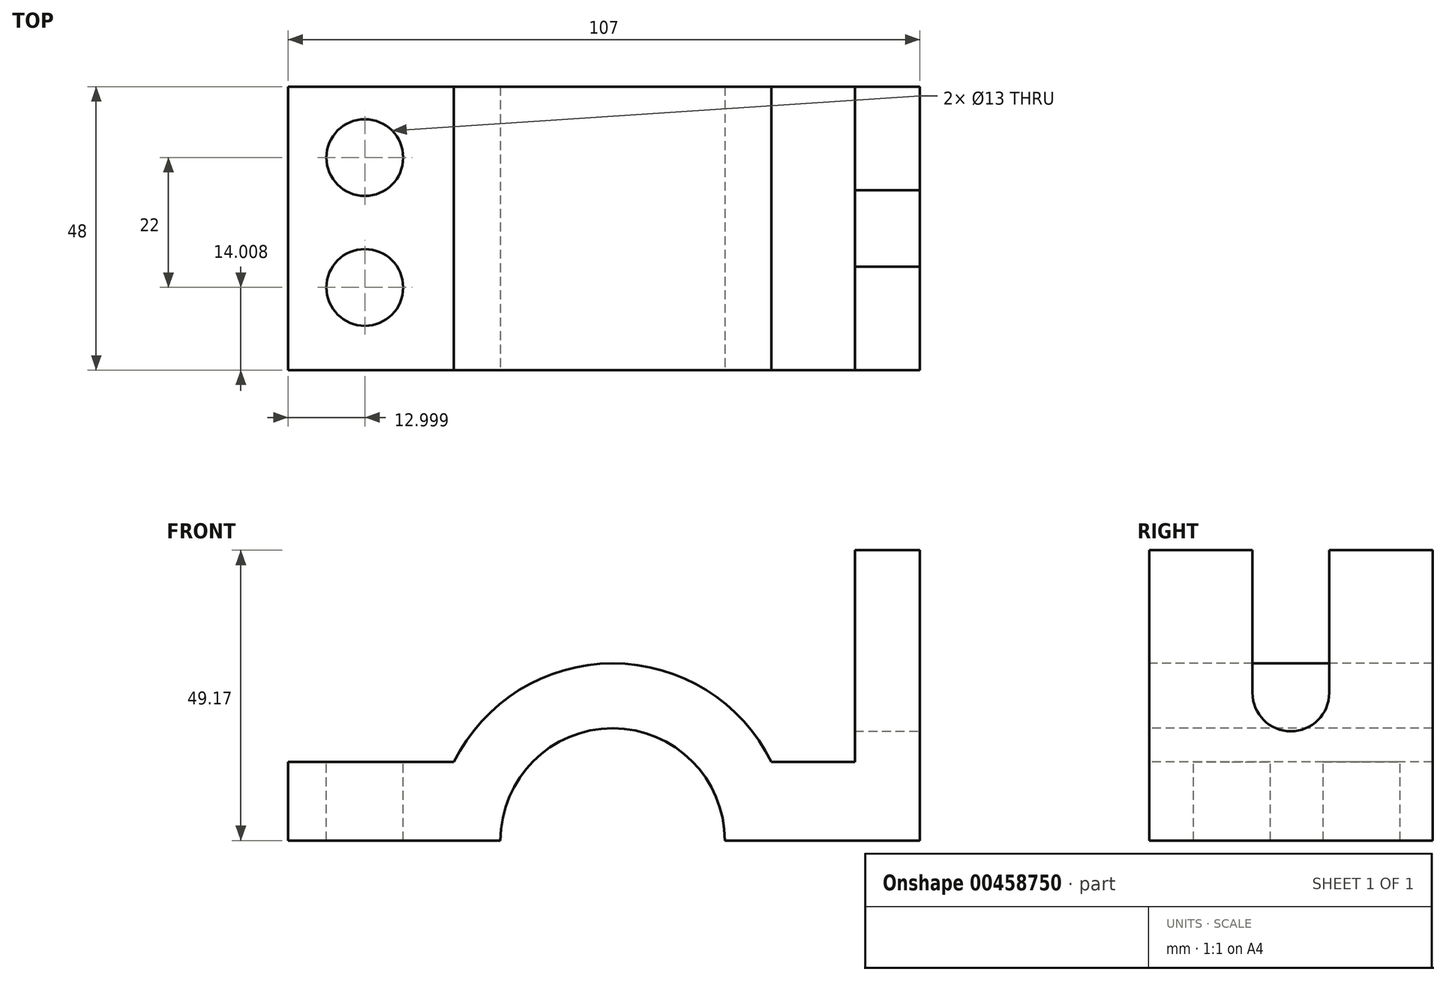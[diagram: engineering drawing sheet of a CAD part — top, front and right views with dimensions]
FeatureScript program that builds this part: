
annotation { "Feature Type Name" : "Feature", "Feature Type Description" : "" }
export const myFeature = defineFeature(function(context is Context, id is Id, definition is map)
    precondition{}
    {
        {
            var Q0;
            Q0=qCreatedBy(makeId("Front.planeOp"),FACE);
            var sketch = newSketch(context, id + "F0", { "sketchPlane" : qUnion([Q0])});
            skLineSegment(sketch, "E0", {"start": v(-19, 0) * mm, "end": v(-54.98, 0) * mm});
            skLineSegment(sketch, "E1", {"start": v(-54.98, 0) * mm, "end": v(-54.98, 13.3) * mm});
            skLineSegment(sketch, "E2", {"start": v(-54.98, 13.3) * mm, "end": v(-26.9, 13.3) * mm});
            skLineSegment(sketch, "E3", {"start": v(19, 0) * mm, "end": v(52.02, 0) * mm});
            skLineSegment(sketch, "E4", {"start": v(52.02, 0) * mm, "end": v(52.02, 49.17) * mm});
            skLineSegment(sketch, "E5", {"start": v(52.02, 49.17) * mm, "end": v(41.02, 49.17) * mm});
            skLineSegment(sketch, "E6", {"start": v(41.02, 49.17) * mm, "end": v(41.02, 13.3) * mm});
            skLineSegment(sketch, "E7", {"start": v(41.02, 13.3) * mm, "end": v(26.9, 13.3) * mm});
            skArc(sketch, "E8", {"start": v(19, 0) * mm, "mid": v(0, 19) * mm, "end": v(-19, 0) * mm});
            skArc(sketch, "E9", {"start": v(26.9, 13.3) * mm, "mid": v(0, 30) * mm, "end": v(-26.9, 13.3) * mm});
            skSolve(sketch);
        }
        {
            var Q0;
            Q0 = qSketchRegion(id + "F0", true);
            extrude(context, id + "F1", {"entities" : qUnion([Q0]), "oppositeDirection" : true, "depth" : 48 * mm});
        }
        {
            var Q0;
            Q0=makeQuery(id+"F1.opExtrude","SWEPT_FACE",FACE,{"disambiguationData":[OSD([sQuery(id+"F0.wireOp",EDGE,"E4")])]});
            var sketch = newSketch(context, id + "F2", { "sketchPlane" : qUnion([Q0])});
            skLineSegment(sketch, "E10", {"start": v(17.5, 49.17) * mm, "end": v(17.5, 25) * mm});
            skLineSegment(sketch, "E11", {"start": v(30.5, 49.17) * mm, "end": v(30.5, 25) * mm});
            skArc(sketch, "E12", {"start": v(17.5, 25) * mm, "mid": v(24, 18.5) * mm, "end": v(30.5, 25) * mm});
            skSolve(sketch);
        }
        {
            var Q0;
            {var subQ0=sQuery(id+"F2.wireOp",EDGE,"E10");Q0=makeQuery(id+"F2.imprint","IMPRINT",FACE,{"disambiguationData":[TD([[makeQuery(id+"F2.imprint","IMPRINT",EDGE,{"derivedFrom":subQ0}),1.0]])]});}
            extrude(context, id + "F3", {"entities" : qUnion([Q0]), "operationType" : NewBodyOperationType.REMOVE, "oppositeDirection" : true, "depth" : 11 * mm});
        }
        {
            var Q0;
            Q0=makeQuery(id+"F1.opExtrude","SWEPT_FACE",FACE,{"disambiguationData":[OSD([sQuery(id+"F0.wireOp",EDGE,"E2")])]});
            var sketch = newSketch(context, id + "F4", { "sketchPlane" : qUnion([Q0])});
            skLineSegment(sketch, "E13.0", {"start": v(-26.9, 48) * mm, "end": v(-26.9, 0) * mm});
            skLineSegment(sketch, "E13.1", {"start": v(-54.98, 48) * mm, "end": v(-26.9, 48) * mm});
            skLineSegment(sketch, "E13.2", {"start": v(-54.98, 48) * mm, "end": v(-54.98, 0) * mm});
            skLineSegment(sketch, "E13.3", {"start": v(-54.98, 0) * mm, "end": v(-26.9, 0) * mm});
            skCircle(sketch, "E14", {"center": v(-41.98, 36) * mm, "radius": 6.5 * mm});
            skCircle(sketch, "E15", {"center": v(-41.98, 14) * mm, "radius": 6.5 * mm});
            skSolve(sketch);
        }
        {
            var Q0;
            Q0=makeQuery(id+"F4.imprint","IMPRINT",FACE,{"disambiguationData":[TD([[makeQuery(id+"F4.imprint","IMPRINT",EDGE,{"derivedFrom":sQuery(id+"F4.wireOp",EDGE,"E14")}),1.0]])]});
            var Q1;
            Q1=makeQuery(id+"F4.imprint","IMPRINT",FACE,{"disambiguationData":[TD([[makeQuery(id+"F4.imprint","IMPRINT",EDGE,{"derivedFrom":sQuery(id+"F4.wireOp",EDGE,"E15")}),1.0]])]});
            extrude(context, id + "F5", {"entities" : qUnion([Q0, Q1]), "operationType" : NewBodyOperationType.REMOVE, "endBound" : BoundingType.THROUGH_ALL, "oppositeDirection" : true, "depth" : 25 * mm});
        }
    });
